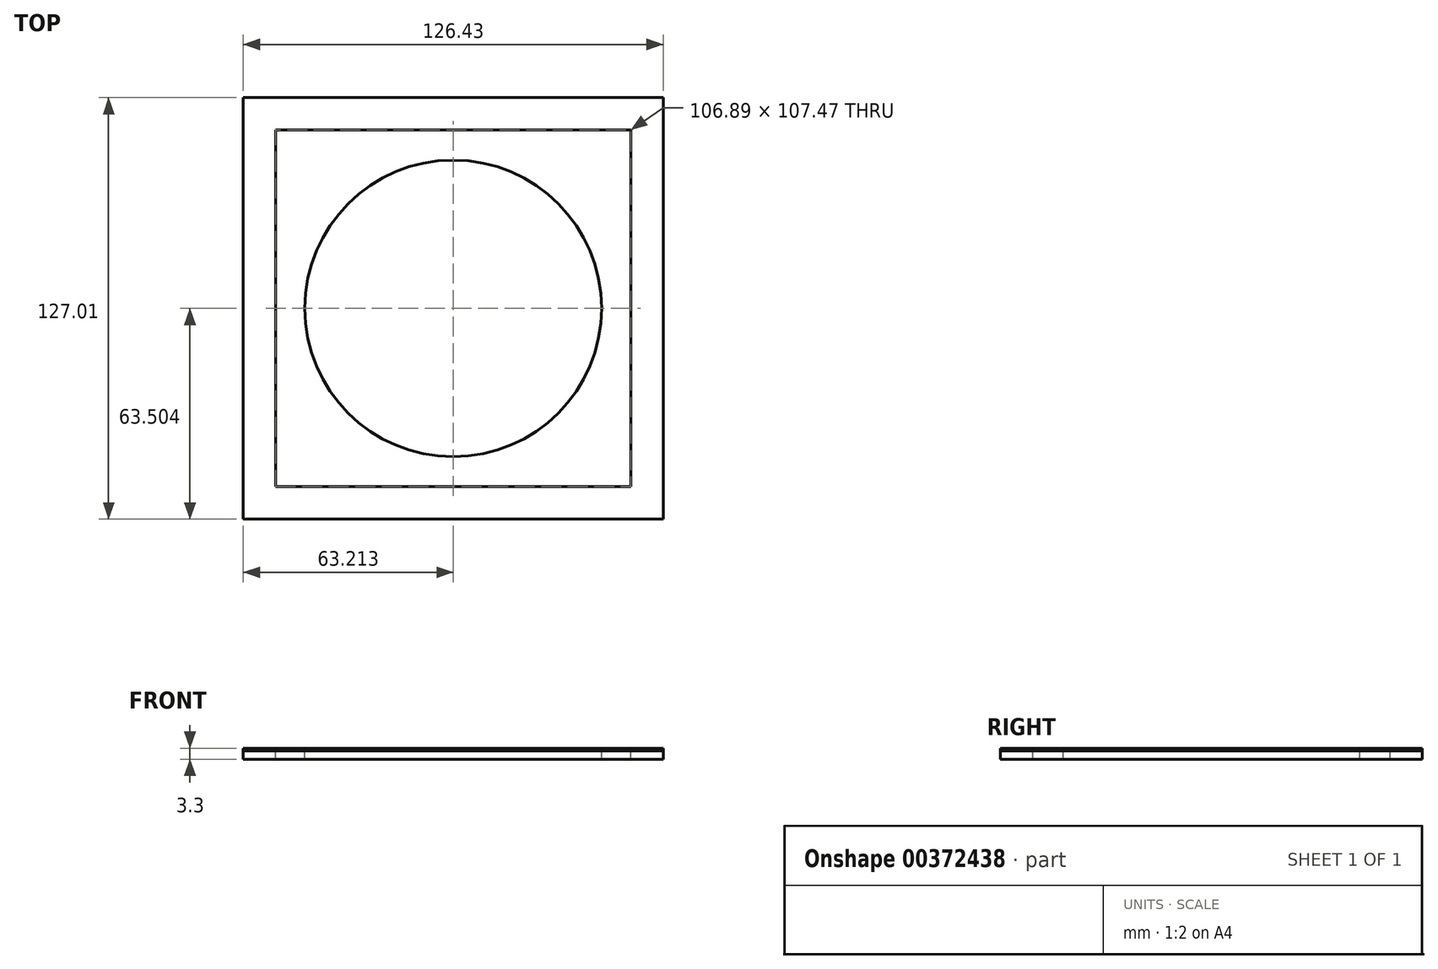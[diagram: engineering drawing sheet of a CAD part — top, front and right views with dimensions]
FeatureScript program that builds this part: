
annotation { "Feature Type Name" : "Feature", "Feature Type Description" : "" }
export const myFeature = defineFeature(function(context is Context, id is Id, definition is map)
    precondition{}
    {
        {
            var Q0;
            Q0=qCreatedBy(makeId("Top.planeOp"),FACE);
            var sketch = newSketch(context, id + "F0", { "sketchPlane" : qUnion([Q0])});
            skLineSegment(sketch, "E0.bottom", {"start": v(8.5, 8.33) * mm, "end": v(66.02, 8.33) * mm});
            skLineSegment(sketch, "E0.top", {"start": v(8.5, 66.1) * mm, "end": v(66.02, 66.1) * mm});
            skLineSegment(sketch, "E0.left", {"start": v(8.5, 8.33) * mm, "end": v(8.5, 66.1) * mm});
            skLineSegment(sketch, "E0.right", {"start": v(66.02, 8.33) * mm, "end": v(66.02, 66.1) * mm});
            skLineSegment(sketch, "E1", {"start": v(37.26, 66.1) * mm, "end": v(37.26, 8.33) * mm, "construction": true});
            skCircle(sketch, "E2", {"center": v(37.26, 37.22) * mm, "radius": 20.32 * mm});
            skLineSegment(sketch, "E3.bottom", {"start": v(12.94, 61.66) * mm, "end": v(61.57, 61.66) * mm});
            skLineSegment(sketch, "E3.top", {"start": v(12.94, 12.77) * mm, "end": v(61.57, 12.77) * mm});
            skLineSegment(sketch, "E3.left", {"start": v(12.94, 61.66) * mm, "end": v(12.94, 12.77) * mm});
            skLineSegment(sketch, "E3.right", {"start": v(61.57, 61.66) * mm, "end": v(61.57, 12.77) * mm});
            skSolve(sketch);
        }
        {
            var Q0;
            Q0=makeQuery(id+"F0.imprint","IMPRINT",FACE,{"disambiguationData":[TD([[makeQuery(id+"F0.imprint","IMPRINT",EDGE,{"derivedFrom":sQuery(id+"F0.wireOp",EDGE,"E2")}),1.0]])]});
            var Q1;
            Q1=makeQuery(id+"F0.imprint","IMPRINT",FACE,{"disambiguationData":[TD([[makeQuery(id+"F0.imprint","IMPRINT",EDGE,{"derivedFrom":sQuery(id+"F0.wireOp",EDGE,"E0.bottom")}),1.0]])]});
            extrude(context, id + "F1", {"entities" : qUnion([Q0, Q1]), "oppositeDirection" : true, "depth" : 1.5 * mm});
        }
        {
            var Q0;
            Q0=makeQuery(id+"F1.opExtrude","SWEPT_BODY",BODY,{"disambiguationData":[OSD([sQuery(id+"F0.wireOp",EDGE,"E0.bottom"),sQuery(id+"F0.wireOp",EDGE,"E0.top"),sQuery(id+"F0.wireOp",EDGE,"E0.left"),sQuery(id+"F0.wireOp",EDGE,"E0.right"),sQuery(id+"F0.wireOp",EDGE,"E3.bottom"),sQuery(id+"F0.wireOp",EDGE,"E3.top"),sQuery(id+"F0.wireOp",EDGE,"E3.left"),sQuery(id+"F0.wireOp",EDGE,"E3.right")])]});
            var Q1;
            Q1=makeQuery(id+"F1.opExtrude","SWEPT_BODY",BODY,{"disambiguationData":[OSD([sQuery(id+"F0.wireOp",EDGE,"E2")])]});
            var Q2;
            Q2=qCreatedBy(makeId("Origin.pointOp"),VERTEX);
            transform(context, id + "F2", {"entities" : qUnion([Q0, Q1]), "transformType" : TransformType.SCALE_UNIFORMLY, "scale" : 2.2, "scalePoint" : qUnion([Q2]), "makeCopy" : false});
        }
        {
            var Q0;
            Q0=makeQuery(id+"F1.opExtrude","SWEPT_BODY",BODY,{"disambiguationData":[OSD([sQuery(id+"F0.wireOp",EDGE,"E0.bottom"),sQuery(id+"F0.wireOp",EDGE,"E0.top"),sQuery(id+"F0.wireOp",EDGE,"E0.left"),sQuery(id+"F0.wireOp",EDGE,"E0.right"),sQuery(id+"F0.wireOp",EDGE,"E3.bottom"),sQuery(id+"F0.wireOp",EDGE,"E3.top"),sQuery(id+"F0.wireOp",EDGE,"E3.left"),sQuery(id+"F0.wireOp",EDGE,"E3.right")])]});
            var Q1;
            Q1=makeQuery(id+"F1.opExtrude","SWEPT_BODY",BODY,{"disambiguationData":[OSD([sQuery(id+"F0.wireOp",EDGE,"E2")])]});
            var Q2;
            Q2=makeQuery(id+"F1.opExtrude","CAP_VERTEX",VERTEX,{"disambiguationData":[OSD([sQuery(id+"F0.wireOp",EDGE,"E0.bottom"),sQuery(id+"F0.wireOp",EDGE,"E0.left")])],"isStart":false});
            var Q3;
            Q3=qCreatedBy(makeId("Origin.pointOp"),VERTEX);
            transform(context, id + "F3", {"entities" : qUnion([Q0, Q1]), "transformType" : TransformType.TRANSLATION_ENTITY, "oppositeDirectionEntity" : false, "transformLine" : qUnion([Q2, Q3]), "makeCopy" : false});
        }
        {
            var Q0;
            Q0=makeQuery(id+"F1.opExtrude","CAP_FACE",FACE,{"disambiguationData":[OSD([sQuery(id+"F0.wireOp",EDGE,"E2")])],"isStart":false});
            var sketch = newSketch(context, id + "F4", { "sketchPlane" : qUnion([Q0])});
            skLineSegment(sketch, "E4.bottom", {"start": v(0, 0) * mm, "end": v(126.43, 0) * mm});
            skLineSegment(sketch, "E4.top", {"start": v(0, -127) * mm, "end": v(126.43, -127) * mm});
            skLineSegment(sketch, "E4.left", {"start": v(0, -127) * mm, "end": v(0, 0) * mm});
            skLineSegment(sketch, "E4.right", {"start": v(126.43, -127) * mm, "end": v(126.43, 0) * mm});
            skSolve(sketch);
        }
        {
            var Q0;
            Q0 = qSketchRegion(id + "F4", true);
            extrude(context, id + "F5", {"entities" : qUnion([Q0]), "oppositeDirection" : true, "depth" : 2.54 * mm});
        }
    });
